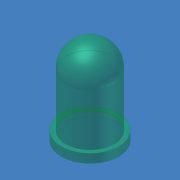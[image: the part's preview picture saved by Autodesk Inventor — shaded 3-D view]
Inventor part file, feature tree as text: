
AUTODESK INVENTOR PART (.ipt)
format: ipt  version: 2011 SP1 (Build 150282100, 282)  size: 102,912 bytes
history: native  units: mm (DEFAULTED — no unit token found)
features: revolve x1, sketch x1
ambient origin geometry x8: Origin, YZ Plane, XZ Plane, XY Plane, X Axis, Y Axis, Z Axis, Center Point
bodies: Solid1 (feature_tree)
feature tree (2):
  revolve  "Revolution1"  [1 undecoded]
  sketch  "Sketch1"  dims[d0=5.0mm d1=9.0mm d2=0.9mm d3=2.95mm d4=90.0deg]
note: 1 required parameter value undecoded (feature->parameter linkage not recoverable at this tier; creation-order binding heuristic only, values carry confidence <= 0.55)
